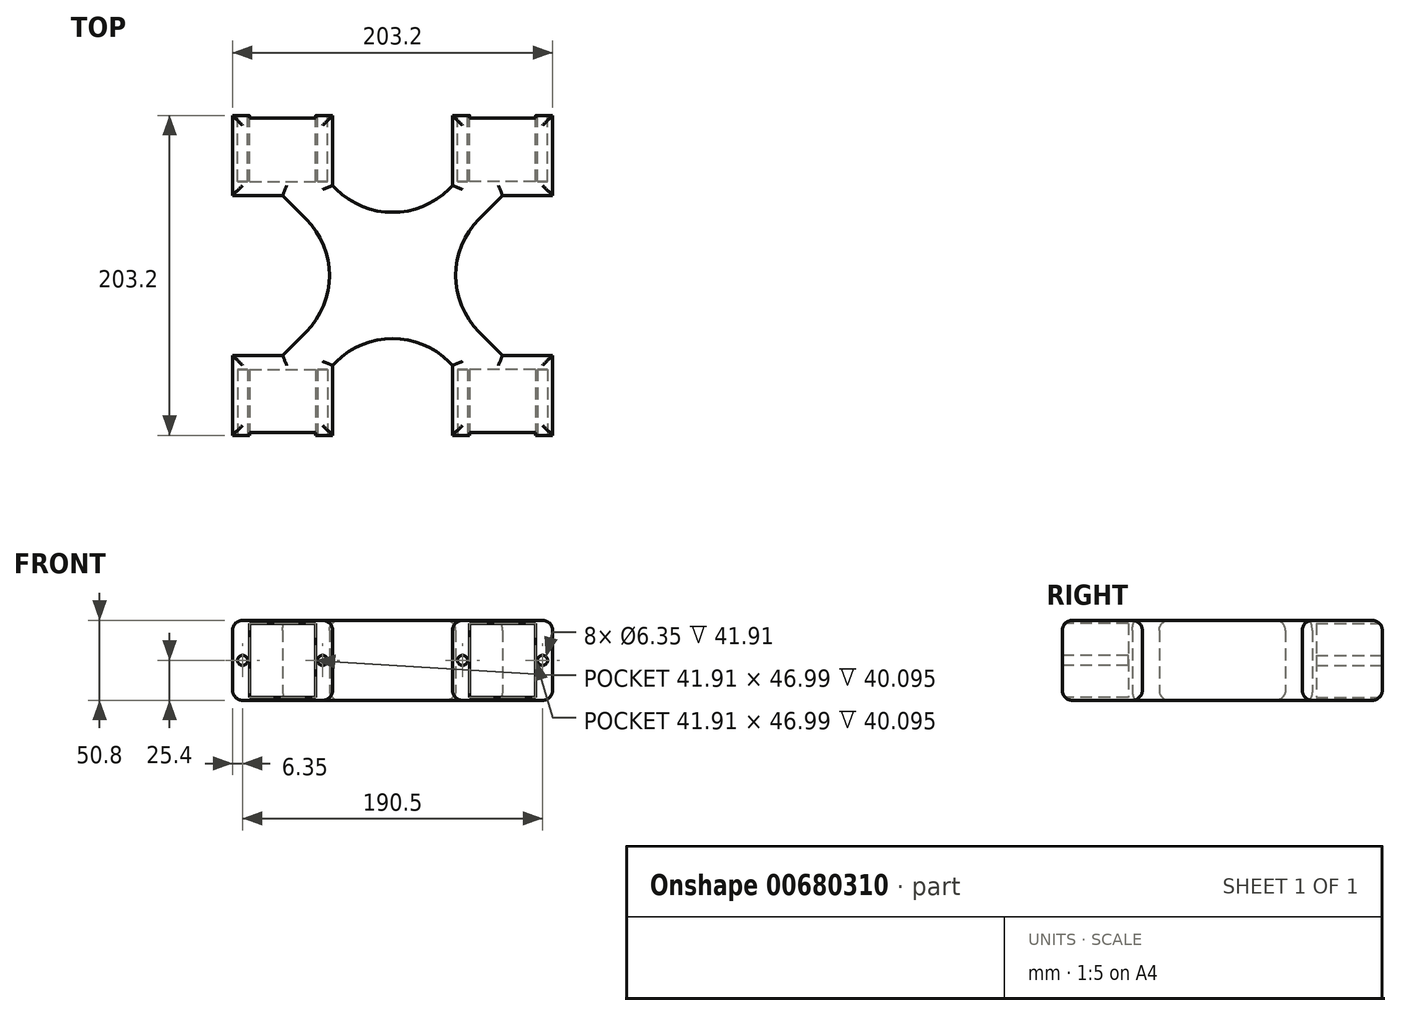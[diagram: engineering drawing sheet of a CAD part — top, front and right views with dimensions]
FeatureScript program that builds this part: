
annotation { "Feature Type Name" : "Feature", "Feature Type Description" : "" }
export const myFeature = defineFeature(function(context is Context, id is Id, definition is map)
    precondition{}
    {
        {
            var Q0;
            Q0=qCreatedBy(makeId("Top.planeOp"),FACE);
            var sketch = newSketch(context, id + "F0", { "sketchPlane" : qUnion([Q0])});
            skLineSegment(sketch, "E0.bottom", {"start": v(-101.6, 101.6) * mm, "end": v(101.6, 101.6) * mm, "construction": true});
            skLineSegment(sketch, "E0.top", {"start": v(-101.6, -101.6) * mm, "end": v(-38.1, -101.6) * mm});
            skLineSegment(sketch, "E0.left", {"start": v(-101.6, 101.6) * mm, "end": v(-101.6, 50.8) * mm});
            skLineSegment(sketch, "E0.right", {"start": v(101.6, 101.6) * mm, "end": v(101.6, -101.6) * mm, "construction": true});
            skPoint(sketch, "E1", {"position": v(101.6, 0) * mm});
            skPoint(sketch, "E2", {"position": v(0, 101.6) * mm});
            skLineSegment(sketch, "E3.bottom", {"start": v(-101.6, 101.6) * mm, "end": v(-38.1, 101.6) * mm, "construction": true});
            skLineSegment(sketch, "E3.top", {"start": v(-101.6, 50.8) * mm, "end": v(-38.1, 50.8) * mm, "construction": true});
            skLineSegment(sketch, "E3.left", {"start": v(-101.6, 101.6) * mm, "end": v(-101.6, 50.8) * mm, "construction": true});
            skLineSegment(sketch, "E3.right", {"start": v(-38.1, 101.6) * mm, "end": v(-38.1, 50.8) * mm, "construction": true});
            skLineSegment(sketch, "E4.MirrorCS", {"start": v(38.1, 101.6) * mm, "end": v(38.1, 50.8) * mm, "construction": true});
            skLineSegment(sketch, "E5.MirrorCS", {"start": v(101.6, 50.8) * mm, "end": v(38.1, 50.8) * mm, "construction": true});
            skLineSegment(sketch, "E6.MirrorCS", {"start": v(-101.6, -50.8) * mm, "end": v(-38.1, -50.8) * mm, "construction": true});
            skLineSegment(sketch, "E7.MirrorCS", {"start": v(38.1, -101.6) * mm, "end": v(38.1, -50.8) * mm, "construction": true});
            skLineSegment(sketch, "E8.MirrorCS", {"start": v(-38.1, -101.6) * mm, "end": v(-38.1, -50.8) * mm, "construction": true});
            skLineSegment(sketch, "E9.MirrorCS", {"start": v(101.6, -50.8) * mm, "end": v(38.1, -50.8) * mm, "construction": true});
            skLineSegment(sketch, "E10.MirrorCS", {"start": v(-101.6, -101.6) * mm, "end": v(-101.6, -50.8) * mm, "construction": true});
            skLineSegment(sketch, "E11.MirrorCS", {"start": v(-101.6, -101.6) * mm, "end": v(-38.1, -101.6) * mm, "construction": true});
            skPoint(sketch, "E12.MirrorP", {"position": v(0, -101.6) * mm});
            skLineSegment(sketch, "E13", {"start": v(-69.85, 50.8) * mm, "end": v(38.1, -57.15) * mm});
            skPoint(sketch, "E14", {"position": v(-69.85, 50.8) * mm});
            skLineSegment(sketch, "E15.MirrorCS", {"start": v(69.85, 50.8) * mm, "end": v(-38.1, -57.15) * mm});
            skLineSegment(sketch, "E16.MirrorCS", {"start": v(69.85, -50.8) * mm, "end": v(-38.1, 57.15) * mm});
            skLineSegment(sketch, "E17.MirrorCS", {"start": v(-69.85, -50.8) * mm, "end": v(38.1, 57.15) * mm});
            skLineSegment(sketch, "E18", {"start": v(-101.6, -50.8) * mm, "end": v(-69.85, -50.8) * mm});
            skLineSegment(sketch, "E19", {"start": v(-38.1, -57.15) * mm, "end": v(-38.1, -101.6) * mm});
            skLineSegment(sketch, "E20", {"start": v(38.1, -57.15) * mm, "end": v(38.1, -101.6) * mm});
            skLineSegment(sketch, "E21", {"start": v(69.85, -50.8) * mm, "end": v(101.6, -50.8) * mm});
            skLineSegment(sketch, "E22", {"start": v(69.85, 50.8) * mm, "end": v(101.6, 50.8) * mm});
            skLineSegment(sketch, "E23", {"start": v(38.1, 57.15) * mm, "end": v(38.1, 101.6) * mm});
            skLineSegment(sketch, "E24", {"start": v(-38.1, 57.15) * mm, "end": v(-38.1, 101.6) * mm});
            skLineSegment(sketch, "E25", {"start": v(-69.85, 50.8) * mm, "end": v(-101.6, 50.8) * mm});
            skLineSegment(sketch, "E26.trimOffspring", {"start": v(-101.6, -50.8) * mm, "end": v(-101.6, -101.6) * mm});
            skLineSegment(sketch, "E27", {"start": v(101.6, 101.6) * mm, "end": v(101.6, 50.8) * mm});
            skLineSegment(sketch, "E28", {"start": v(101.6, -50.8) * mm, "end": v(101.6, -101.6) * mm});
            skLineSegment(sketch, "E29.trimOffspring", {"start": v(38.1, -101.6) * mm, "end": v(101.6, -101.6) * mm});
            skLineSegment(sketch, "E30", {"start": v(-101.6, 101.6) * mm, "end": v(-38.1, 101.6) * mm});
            skLineSegment(sketch, "E31", {"start": v(38.1, 101.6) * mm, "end": v(101.6, 101.6) * mm});
            skSolve(sketch);
        }
        {
            var Q0;
            Q0 = qSketchRegion(id + "F0", true);
            extrude(context, id + "F1", {"entities" : qUnion([Q0]), "depth" : 50.8 * mm, "offsetDistance" : 25.4 * mm});
        }
        {
            var Q0;
            Q0=makeQuery(id+"F1.opExtrude","SWEPT_FACE",FACE,{"disambiguationData":[OSD([sQuery(id+"F0.wireOp",EDGE,"E0.top")])]});
            var sketch = newSketch(context, id + "F2", { "sketchPlane" : qUnion([Q0])});
            skLineSegment(sketch, "E32", {"start": v(-101.6, 25.4) * mm, "end": v(-38.1, 25.4) * mm, "construction": true});
            skCircle(sketch, "E33", {"center": v(-95.25, 25.4) * mm, "radius": 3.18 * mm});
            skLineSegment(sketch, "E34", {"start": v(-69.85, 25.4) * mm, "end": v(-69.85, 79) * mm, "construction": true});
            skCircle(sketch, "E35.MirrorC", {"center": v(-44.45, 25.4) * mm, "radius": 3.18 * mm});
            skCircle(sketch, "E36.MirrorC", {"center": v(44.45, 25.4) * mm, "radius": 3.18 * mm});
            skCircle(sketch, "E37.MirrorC", {"center": v(95.25, 25.4) * mm, "radius": 3.18 * mm});
            skLineSegment(sketch, "E38.bottom", {"start": v(-90.8, 48.9) * mm, "end": v(-48.9, 48.9) * mm});
            skLineSegment(sketch, "E38.top", {"start": v(-90.8, 1.9) * mm, "end": v(-48.9, 1.9) * mm});
            skLineSegment(sketch, "E38.left", {"start": v(-90.8, 48.9) * mm, "end": v(-90.8, 1.9) * mm});
            skLineSegment(sketch, "E38.right", {"start": v(-48.9, 48.9) * mm, "end": v(-48.9, 1.9) * mm});
            skPoint(sketch, "E39", {"position": v(-90.8, 25.4) * mm});
            skPoint(sketch, "E40", {"position": v(-69.85, 48.9) * mm});
            skLineSegment(sketch, "E41.MirrorCS", {"start": v(48.9, 48.9) * mm, "end": v(48.9, 1.9) * mm});
            skLineSegment(sketch, "E42.MirrorCS", {"start": v(90.8, 48.9) * mm, "end": v(48.9, 48.9) * mm});
            skLineSegment(sketch, "E43.MirrorCS", {"start": v(90.8, 1.9) * mm, "end": v(48.9, 1.9) * mm});
            skLineSegment(sketch, "E44.MirrorCS", {"start": v(90.8, 48.9) * mm, "end": v(90.8, 1.9) * mm});
            skSolve(sketch);
        }
        {
            var Q0;
            Q0 = qSketchRegion(id + "F2", true);
            extrude(context, id + "F3", {"entities" : qUnion([Q0]), "operationType" : NewBodyOperationType.REMOVE, "oppositeDirection" : true, "depth" : 41.9 * mm, "offsetDistance" : 25.4 * mm});
        }
        {
            var Q0;
            Q0=makeQuery(id+"F1.opExtrude","SWEPT_FACE",FACE,{"disambiguationData":[OSD([sQuery(id+"F0.wireOp",EDGE,"E30")])]});
            var sketch = newSketch(context, id + "F4", { "sketchPlane" : qUnion([Q0])});
            skCircle(sketch, "E45", {"center": v(95.25, 25.4) * mm, "radius": 3.18 * mm});
            skPoint(sketch, "E45.centerSnap0", {"position": v(101.6, 25.4) * mm});
            skCircle(sketch, "E46", {"center": v(44.45, 25.4) * mm, "radius": 3.18 * mm});
            skLineSegment(sketch, "E47.bottom", {"start": v(90.8, 48.9) * mm, "end": v(48.9, 48.9) * mm});
            skLineSegment(sketch, "E47.top", {"start": v(90.8, 1.9) * mm, "end": v(48.9, 1.9) * mm});
            skLineSegment(sketch, "E47.left", {"start": v(90.8, 48.9) * mm, "end": v(90.8, 1.9) * mm});
            skLineSegment(sketch, "E47.right", {"start": v(48.9, 48.9) * mm, "end": v(48.9, 1.9) * mm});
            skLineSegment(sketch, "E48.MirrorCS", {"start": v(-90.8, 1.9) * mm, "end": v(-48.9, 1.9) * mm});
            skLineSegment(sketch, "E49.MirrorCS", {"start": v(-90.8, 48.9) * mm, "end": v(-48.9, 48.9) * mm});
            skPoint(sketch, "E50.MirrorP", {"position": v(-101.6, 25.4) * mm});
            skLineSegment(sketch, "E51.MirrorCS", {"start": v(-48.9, 48.9) * mm, "end": v(-48.9, 1.9) * mm});
            skLineSegment(sketch, "E52.MirrorCS", {"start": v(-90.8, 48.9) * mm, "end": v(-90.8, 1.9) * mm});
            skCircle(sketch, "E53.MirrorC", {"center": v(-95.25, 25.4) * mm, "radius": 3.18 * mm});
            skCircle(sketch, "E54.MirrorC", {"center": v(-44.45, 25.4) * mm, "radius": 3.18 * mm});
            skSolve(sketch);
        }
        {
            var Q0;
            Q0 = qSketchRegion(id + "F4", true);
            extrude(context, id + "F5", {"entities" : qUnion([Q0]), "operationType" : NewBodyOperationType.REMOVE, "oppositeDirection" : true, "depth" : 41.9 * mm, "offsetDistance" : 25.4 * mm});
        }
        {
            var Q0;
            Q0=makeQuery(id+"F1.opExtrude","SWEPT_EDGE",EDGE,{"disambiguationData":[OSD([sQuery(id+"F0.wireOp",EDGE,"E16.MirrorCS"),sQuery(id+"F0.wireOp",EDGE,"E17.MirrorCS")])]});
            var Q1;
            Q1=makeQuery(id+"F1.opExtrude","SWEPT_EDGE",EDGE,{"disambiguationData":[OSD([sQuery(id+"F0.wireOp",EDGE,"E15.MirrorCS"),sQuery(id+"F0.wireOp",EDGE,"E16.MirrorCS")])]});
            var Q2;
            Q2=makeQuery(id+"F1.opExtrude","SWEPT_EDGE",EDGE,{"disambiguationData":[OSD([sQuery(id+"F0.wireOp",EDGE,"E13"),sQuery(id+"F0.wireOp",EDGE,"E17.MirrorCS")])]});
            var Q3;
            Q3=makeQuery(id+"F1.opExtrude","SWEPT_EDGE",EDGE,{"disambiguationData":[OSD([sQuery(id+"F0.wireOp",EDGE,"E13"),sQuery(id+"F0.wireOp",EDGE,"E15.MirrorCS")])]});
            fillet(context, id + "F6", {"entities" : qUnion([Q0, Q1, Q2, Q3]), "radius" : 50.8 * mm, "tangentPropagation" : true, "allowEdgeOverflow" : false});
        }
        {
            var Q0;
            Q0=makeQuery(id+"F1.opExtrude","CAP_FACE",FACE,{"disambiguationData":[OSD([sQuery(id+"F0.wireOp",EDGE,"E0.left"),sQuery(id+"F0.wireOp",EDGE,"E0.top"),sQuery(id+"F0.wireOp",EDGE,"E13"),sQuery(id+"F0.wireOp",EDGE,"E15.MirrorCS"),sQuery(id+"F0.wireOp",EDGE,"E16.MirrorCS"),sQuery(id+"F0.wireOp",EDGE,"E17.MirrorCS"),sQuery(id+"F0.wireOp",EDGE,"E18"),sQuery(id+"F0.wireOp",EDGE,"E19"),sQuery(id+"F0.wireOp",EDGE,"E20"),sQuery(id+"F0.wireOp",EDGE,"E21"),sQuery(id+"F0.wireOp",EDGE,"E22"),sQuery(id+"F0.wireOp",EDGE,"E23"),sQuery(id+"F0.wireOp",EDGE,"E24"),sQuery(id+"F0.wireOp",EDGE,"E25"),sQuery(id+"F0.wireOp",EDGE,"E26.trimOffspring"),sQuery(id+"F0.wireOp",EDGE,"E27"),sQuery(id+"F0.wireOp",EDGE,"E28"),sQuery(id+"F0.wireOp",EDGE,"E29.trimOffspring"),sQuery(id+"F0.wireOp",EDGE,"E30"),sQuery(id+"F0.wireOp",EDGE,"E31")])],"isStart":true});
            var Q1;
            Q1=makeQuery(id+"F1.opExtrude","CAP_FACE",FACE,{"disambiguationData":[OSD([sQuery(id+"F0.wireOp",EDGE,"E0.left"),sQuery(id+"F0.wireOp",EDGE,"E0.top"),sQuery(id+"F0.wireOp",EDGE,"E13"),sQuery(id+"F0.wireOp",EDGE,"E15.MirrorCS"),sQuery(id+"F0.wireOp",EDGE,"E16.MirrorCS"),sQuery(id+"F0.wireOp",EDGE,"E17.MirrorCS"),sQuery(id+"F0.wireOp",EDGE,"E18"),sQuery(id+"F0.wireOp",EDGE,"E19"),sQuery(id+"F0.wireOp",EDGE,"E20"),sQuery(id+"F0.wireOp",EDGE,"E21"),sQuery(id+"F0.wireOp",EDGE,"E22"),sQuery(id+"F0.wireOp",EDGE,"E23"),sQuery(id+"F0.wireOp",EDGE,"E24"),sQuery(id+"F0.wireOp",EDGE,"E25"),sQuery(id+"F0.wireOp",EDGE,"E26.trimOffspring"),sQuery(id+"F0.wireOp",EDGE,"E27"),sQuery(id+"F0.wireOp",EDGE,"E28"),sQuery(id+"F0.wireOp",EDGE,"E29.trimOffspring"),sQuery(id+"F0.wireOp",EDGE,"E30"),sQuery(id+"F0.wireOp",EDGE,"E31")])],"isStart":false});
            fillet(context, id + "F7", {"entities" : qUnion([Q0, Q1]), "radius" : 6.35 * mm, "tangentPropagation" : true, "allowEdgeOverflow" : false});
        }
    });
